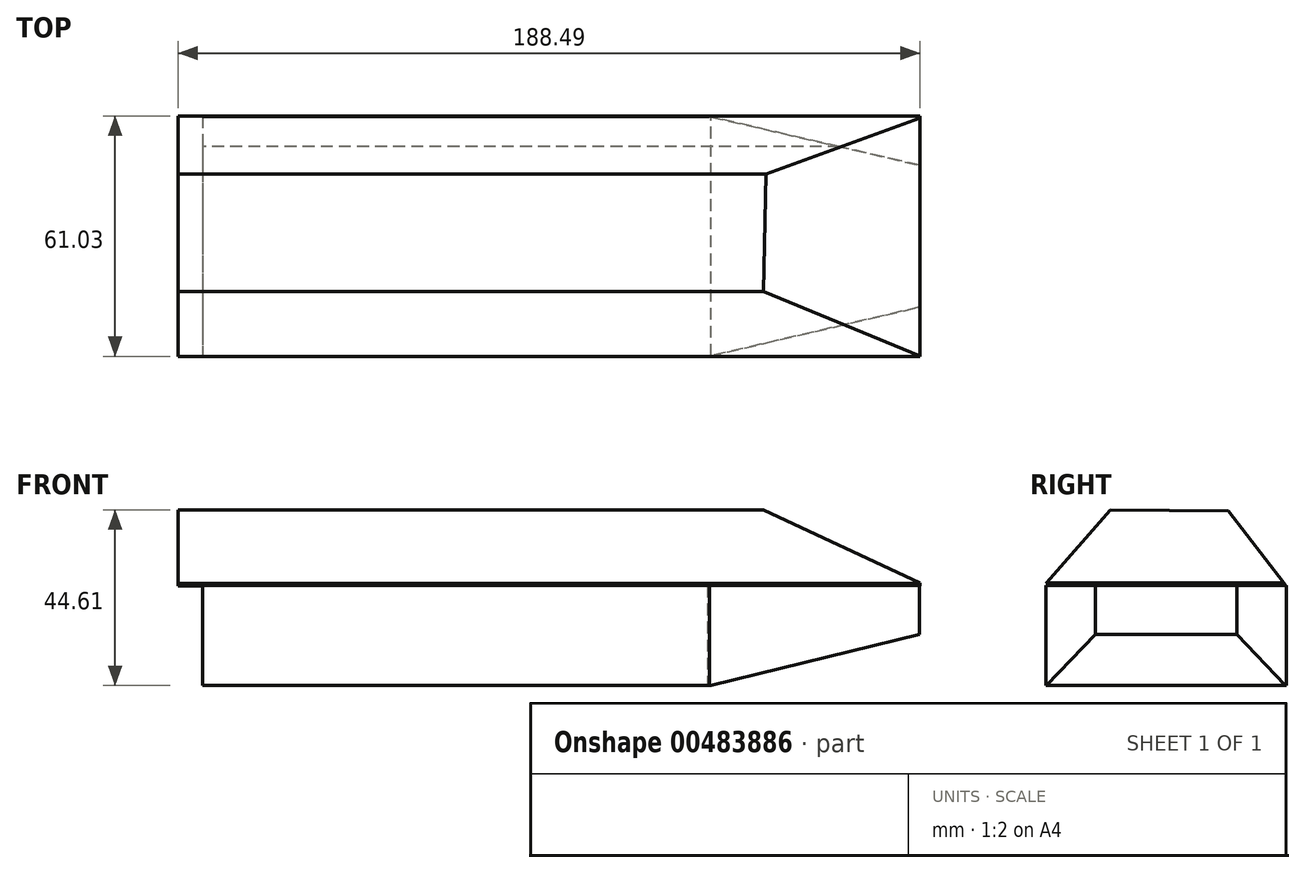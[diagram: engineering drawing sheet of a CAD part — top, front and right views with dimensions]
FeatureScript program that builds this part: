
annotation { "Feature Type Name" : "Feature", "Feature Type Description" : "" }
export const myFeature = defineFeature(function(context is Context, id is Id, definition is map)
    precondition{}
    {
        {
            var Q0;
            Q0=qCreatedBy(makeId("Top.planeOp"),FACE);
            var sketch = newSketch(context, id + "F0", { "sketchPlane" : qUnion([Q0])});
            skLineSegment(sketch, "E0.bottom", {"start": v(-95.31, 31.1) * mm, "end": v(32.9, 31.1) * mm});
            skLineSegment(sketch, "E0.top", {"start": v(-95.31, -29.91) * mm, "end": v(33.37, -29.91) * mm});
            skLineSegment(sketch, "E0.left", {"start": v(-95.31, 31.1) * mm, "end": v(-95.31, -29.91) * mm});
            skLineSegment(sketch, "E1", {"start": v(33.37, -29.91) * mm, "end": v(86.78, -17.42) * mm});
            skLineSegment(sketch, "E2", {"start": v(86.78, -17.42) * mm, "end": v(86.78, 18.64) * mm});
            skLineSegment(sketch, "E3", {"start": v(86.78, 18.64) * mm, "end": v(32.9, 31.1) * mm});
            skSolve(sketch);
        }
        {
            var Q0;
            Q0=makeQuery(id+"F0.imprint","IMPRINT",FACE,{"disambiguationData":[TD([[makeQuery(id+"F0.imprint","IMPRINT",EDGE,{"derivedFrom":sQuery(id+"F0.wireOp",EDGE,"E0.bottom")}),-1.0]])]});
            extrude(context, id + "F1", {"entities" : qUnion([Q0]), "depth" : 25.4 * mm});
        }
        {
            var Q0;
            Q0=qCreatedBy(makeId("Right.planeOp"),FACE);
            var sketch = newSketch(context, id + "F2", { "sketchPlane" : qUnion([Q0])});
            skLineSegment(sketch, "E4", {"start": v(-29.93, 25.9) * mm, "end": v(-13.53, 44.6) * mm});
            skLineSegment(sketch, "E5", {"start": v(31.08, 25.33) * mm, "end": v(16.4, 44.32) * mm});
            skLineSegment(sketch, "E6", {"start": v(16.4, 44.32) * mm, "end": v(-13.53, 44.6) * mm});
            skLineSegment(sketch, "E7", {"start": v(-29.93, 25.9) * mm, "end": v(31.08, 25.33) * mm});
            skSolve(sketch);
        }
        {
            var Q0;
            Q0=makeQuery(id+"F2.imprint","IMPRINT",FACE,{"disambiguationData":[TD([[makeQuery(id+"F2.imprint","IMPRINT",EDGE,{"derivedFrom":sQuery(id+"F2.wireOp",EDGE,"E4")}),-1.0]])]});
            extrude(context, id + "F3", {"entities" : qUnion([Q0]), "operationType" : NewBodyOperationType.ADD, "endBound" : BoundingType.SYMMETRIC, "depth" : 203.2 * mm});
        }
        {
            var Q0;
            Q0=qCreatedBy(makeId("Front.planeOp"),FACE);
            var sketch = newSketch(context, id + "F4", { "sketchPlane" : qUnion([Q0])});
            skLineSegment(sketch, "E8.bottom", {"start": v(86.89, 0) * mm, "end": v(110.3, 0) * mm});
            skLineSegment(sketch, "E8.top", {"start": v(87.93, 60.35) * mm, "end": v(110.3, 60.35) * mm});
            skLineSegment(sketch, "E8.right", {"start": v(110.3, 0) * mm, "end": v(110.3, 60.35) * mm});
            skLineSegment(sketch, "E9", {"start": v(86.89, 25.98) * mm, "end": v(13.53, 60.35) * mm});
            skLineSegment(sketch, "E10", {"start": v(13.53, 60.35) * mm, "end": v(87.93, 60.35) * mm});
            skLineSegment(sketch, "E11", {"start": v(86.89, 13) * mm, "end": v(33.82, 0) * mm});
            skLineSegment(sketch, "E12", {"start": v(86.89, 13) * mm, "end": v(86.89, 25.98) * mm});
            skLineSegment(sketch, "E13", {"start": v(33.82, 0) * mm, "end": v(86.89, 0) * mm});
            skSolve(sketch);
        }
        {
            var Q0;
            Q0=makeQuery(id+"F4.imprint","IMPRINT",FACE,{"disambiguationData":[TD([[makeQuery(id+"F4.imprint","IMPRINT",EDGE,{"derivedFrom":sQuery(id+"F4.wireOp",EDGE,"E8.bottom")}),1.0]])]});
            extrude(context, id + "F5", {"entities" : qUnion([Q0]), "operationType" : NewBodyOperationType.REMOVE, "endBound" : BoundingType.SYMMETRIC, "depth" : 254 * mm});
        }
    });
